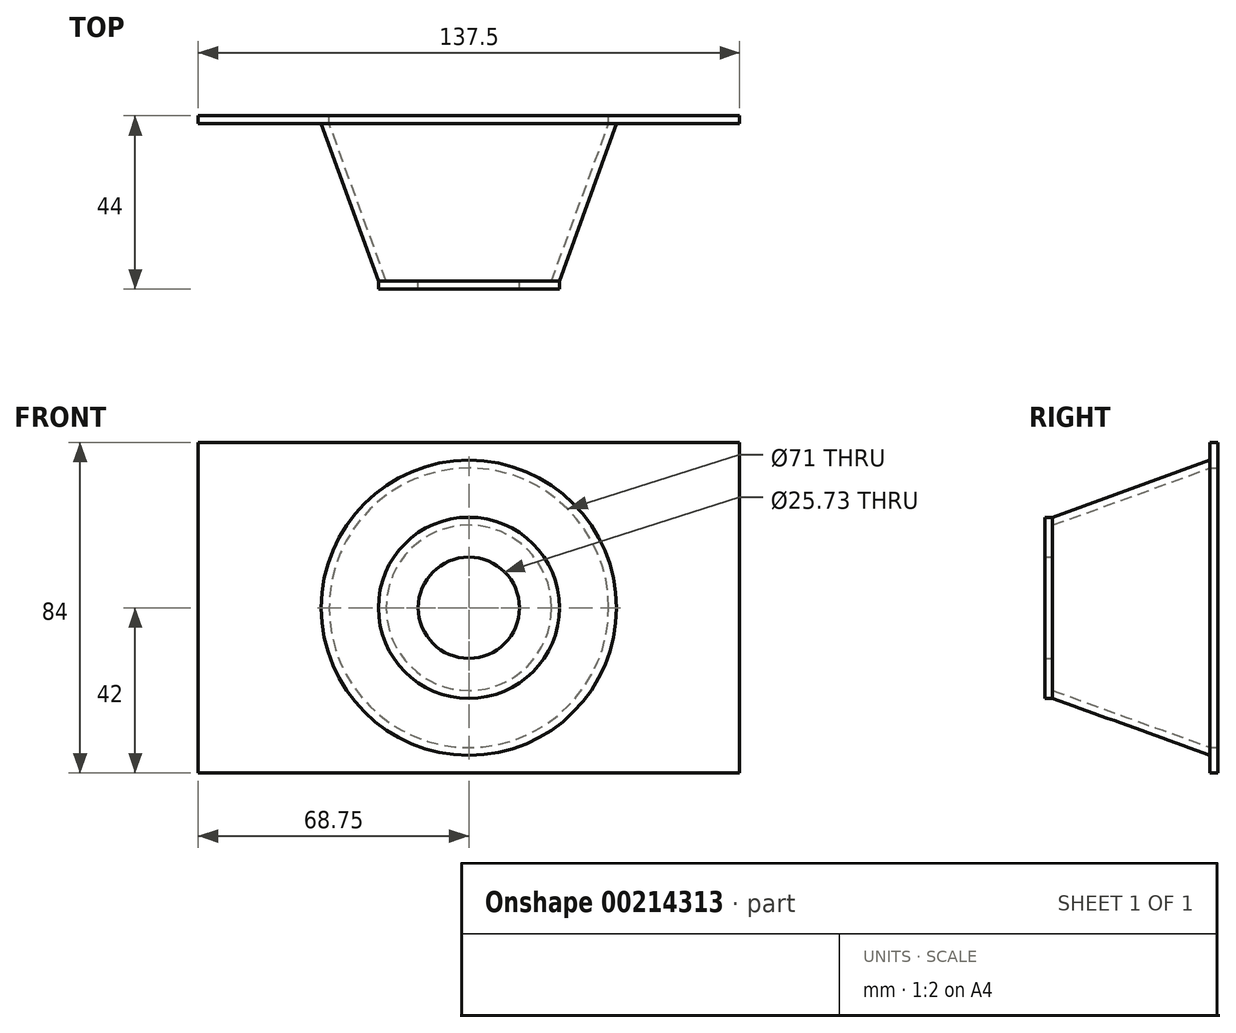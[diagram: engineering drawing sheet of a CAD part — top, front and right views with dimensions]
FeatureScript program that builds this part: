
annotation { "Feature Type Name" : "Feature", "Feature Type Description" : "" }
export const myFeature = defineFeature(function(context is Context, id is Id, definition is map)
    precondition{}
    {
        {
            var Q0;
            Q0=qCreatedBy(makeId("Front.planeOp"),FACE);
            var sketch = newSketch(context, id + "F0", { "sketchPlane" : qUnion([Q0])});
            skLineSegment(sketch, "E0.bottom", {"start": v(68.75, 42) * mm, "end": v(-68.75, 42) * mm});
            skLineSegment(sketch, "E0.top", {"start": v(68.75, -42) * mm, "end": v(-68.75, -42) * mm});
            skLineSegment(sketch, "E0.left", {"start": v(68.75, 42) * mm, "end": v(68.75, -42) * mm});
            skLineSegment(sketch, "E0.right", {"start": v(-68.75, 42) * mm, "end": v(-68.75, -42) * mm});
            skPoint(sketch, "E0.middle", {"position": v(0, 0) * mm});
            skCircle(sketch, "E1", {"center": v(0, 0) * mm, "radius": 35.5 * mm});
            skSolve(sketch);
        }
        {
            var Q0;
            Q0 = qSketchRegion(id + "F0", true);
            extrude(context, id + "F1", {"entities" : qUnion([Q0]), "depth" : 2 * mm});
        }
        {
            var Q0;
            Q0=makeQuery(id+"F1.opExtrude","CAP_FACE",FACE,{"disambiguationData":[OSD([sQuery(id+"F0.wireOp",EDGE,"E0.bottom"),sQuery(id+"F0.wireOp",EDGE,"E0.top"),sQuery(id+"F0.wireOp",EDGE,"E0.left"),sQuery(id+"F0.wireOp",EDGE,"E0.right"),sQuery(id+"F0.wireOp",EDGE,"E1")])],"isStart":false});
            var sketch = newSketch(context, id + "F2", { "sketchPlane" : qUnion([Q0])});
            skCircle(sketch, "E2", {"center": v(0, 0) * mm, "radius": 37.5 * mm});
            skSolve(sketch);
        }
        {
            var Q0;
            Q0=qCreatedBy(makeId("Front.planeOp"),FACE);
            cPlane(context, id + "F3", {"entities" : qUnion([Q0]), "cplaneType" : CPlaneType.OFFSET, "offset" : 42 * mm, "width" : 150 * mm, "height" : 150 * mm});
        }
        {
            var Q0;
            Q0=qCreatedBy(id+"F3.planeOp",FACE);
            var sketch = newSketch(context, id + "F4", { "sketchPlane" : qUnion([Q0])});
            skCircle(sketch, "E3", {"center": v(0, 0) * mm, "radius": 23 * mm});
            skSolve(sketch);
        }
        {
            var Q1;
            Q1 = qSketchRegion(id + "F2", true);
            var Q2;
            Q2 = qSketchRegion(id + "F4", true);
            loft(context, id + "F5", {"operationType" : NewBodyOperationType.ADD, "sheetProfilesArray" : [{ "sheetProfileEntities" : qUnion([Q1]) }, { "sheetProfileEntities" : qUnion([Q2]) }]});
        }
        {
            var Q0;
            Q0=makeQuery(id+"F1.opExtrude","CAP_FACE",FACE,{"disambiguationData":[OSD([sQuery(id+"F0.wireOp",EDGE,"E0.bottom"),sQuery(id+"F0.wireOp",EDGE,"E0.top"),sQuery(id+"F0.wireOp",EDGE,"E0.left"),sQuery(id+"F0.wireOp",EDGE,"E0.right"),sQuery(id+"F0.wireOp",EDGE,"E1")])],"isStart":false});
            var sketch = newSketch(context, id + "F6", { "sketchPlane" : qUnion([Q0])});
            skCircle(sketch, "E4", {"center": v(0, 0) * mm, "radius": 35.5 * mm});
            skSolve(sketch);
        }
        {
            var Q0;
            Q0=makeQuery(id+"F5.opLoft","CAP_FACE",FACE,{"disambiguationData":[OSD([makeQuery(id+"F4.imprint","IMPRINT",FACE,{"disambiguationData":[TD([[makeQuery(id+"F4.imprint","IMPRINT",EDGE,{"derivedFrom":sQuery(id+"F4.wireOp",EDGE,"E3")}),1.0]])]})])],"isStart":true});
            var sketch = newSketch(context, id + "F7", { "sketchPlane" : qUnion([Q0])});
            skCircle(sketch, "E5", {"center": v(0, 0) * mm, "radius": 21 * mm});
            skSolve(sketch);
        }
        {
            var Q1;
            Q1 = qSketchRegion(id + "F6", true);
            var Q2;
            Q2 = qSketchRegion(id + "F7", true);
            loft(context, id + "F8", {"operationType" : NewBodyOperationType.REMOVE, "sheetProfilesArray" : [{ "sheetProfileEntities" : qUnion([Q1]) }, { "sheetProfileEntities" : qUnion([Q2]) }]});
        }
        {
            var Q0;
            Q0=qCreatedBy(id+"F3.planeOp",FACE);
            var sketch = newSketch(context, id + "F9", { "sketchPlane" : qUnion([Q0])});
            skCircle(sketch, "E6", {"center": v(0, 0) * mm, "radius": 23 * mm});
            skCircle(sketch, "E7", {"center": v(0, 0) * mm, "radius": 12.86 * mm});
            skSolve(sketch);
        }
        {
            var Q0;
            Q0 = qSketchRegion(id + "F9", true);
            extrude(context, id + "F10", {"entities" : qUnion([Q0]), "operationType" : NewBodyOperationType.ADD, "depth" : 2 * mm});
        }
    });
